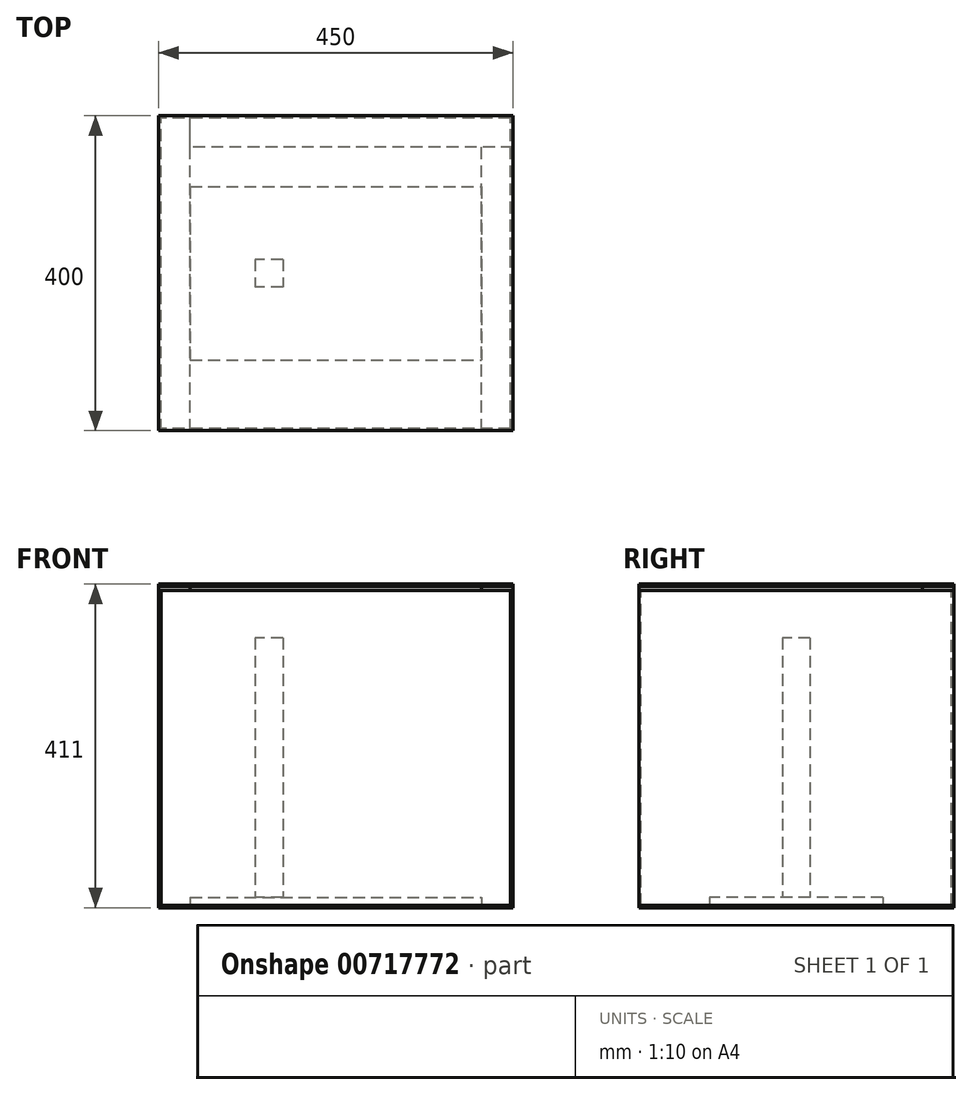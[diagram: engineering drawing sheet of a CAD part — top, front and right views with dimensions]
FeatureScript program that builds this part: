
annotation { "Feature Type Name" : "Feature", "Feature Type Description" : "" }
export const myFeature = defineFeature(function(context is Context, id is Id, definition is map)
    precondition{}
    {
        {
            assignVariable(context, id + "F0", {"name" : "t", "anyValue" : 3});
        }
        {
            var Q0;
            Q0=qCreatedBy(makeId("Top.planeOp"),FACE);
            var sketch = newSketch(context, id + "F1", { "sketchPlane" : qUnion([Q0])});
            skLineSegment(sketch, "E0.bottom", {"start": v(145, 97.5) * mm, "end": v(-145, 97.5) * mm});
            skLineSegment(sketch, "E0.top", {"start": v(145, -97.5) * mm, "end": v(-145, -97.5) * mm});
            skLineSegment(sketch, "E0.left", {"start": v(145, 97.5) * mm, "end": v(145, -97.5) * mm});
            skLineSegment(sketch, "E0.right", {"start": v(-145, 97.5) * mm, "end": v(-145, -97.5) * mm});
            skPoint(sketch, "E0.middle", {"position": v(0, 0) * mm});
            skSolve(sketch);
        }
        {
            var Q0;
            Q0 = qSketchRegion(id + "F1", true);
            extrude(context, id + "F2", {"entities" : qUnion([Q0]), "depth" : 10 * mm, "offsetDistance" : 25 * mm});
        }
        {
            var Q0;
            Q0=qCreatedBy(makeId("Top.planeOp"),FACE);
            var sketch = newSketch(context, id + "F3", { "sketchPlane" : qUnion([Q0])});
            skLineSegment(sketch, "E1.bottom", {"start": v(-185, 110) * mm, "end": v(185, 110) * mm});
            skLineSegment(sketch, "E1.top", {"start": v(-185, -110) * mm, "end": v(185, -110) * mm});
            skLineSegment(sketch, "E1.left", {"start": v(-185, 110) * mm, "end": v(-185, -110) * mm});
            skLineSegment(sketch, "E1.right", {"start": v(185, 110) * mm, "end": v(185, -110) * mm});
            skPoint(sketch, "E1.middle", {"position": v(0, 0) * mm});
            skSolve(sketch);
        }
        {
            var Q0;
            Q0 = qSketchRegion(id + "F3", true);
            extrude(context, id + "F4", {"entities" : qUnion([Q0]), "depth" : 10 * mm, "offsetDistance" : 25 * mm});
        }
        {
            var Q0;
            Q0=makeQuery(id+"F4.opExtrude","CAP_FACE",FACE,{"disambiguationData":[OSD([sQuery(id+"F3.wireOp",EDGE,"E1.bottom"),sQuery(id+"F3.wireOp",EDGE,"E1.top"),sQuery(id+"F3.wireOp",EDGE,"E1.left"),sQuery(id+"F3.wireOp",EDGE,"E1.right")])],"isStart":false});
            var sketch = newSketch(context, id + "F5", { "sketchPlane" : qUnion([Q0])});
            skLineSegment(sketch, "E2.bottom", {"start": v(-67.27, 17.5) * mm, "end": v(-102.27, 17.5) * mm});
            skLineSegment(sketch, "E2.top", {"start": v(-67.27, -17.5) * mm, "end": v(-102.27, -17.5) * mm});
            skLineSegment(sketch, "E2.left", {"start": v(-67.27, 17.5) * mm, "end": v(-67.27, -17.5) * mm});
            skLineSegment(sketch, "E2.right", {"start": v(-102.27, 17.5) * mm, "end": v(-102.27, -17.5) * mm});
            skPoint(sketch, "E2.middle", {"position": v(-84.77, 0) * mm});
            skSolve(sketch);
        }
        {
            var Q0;
            Q0=makeQuery(id+"F5.imprint","IMPRINT",FACE,{"disambiguationData":[TD([[makeQuery(id+"F5.imprint","IMPRINT",EDGE,{"derivedFrom":sQuery(id+"F5.wireOp",EDGE,"E2.bottom")}),1.0]])]});
            extrude(context, id + "F6", {"entities" : qUnion([Q0]), "operationType" : NewBodyOperationType.ADD, "depth" : 330 * mm, "offsetDistance" : 25 * mm});
        }
        {
            var Q0;
            Q0=qCreatedBy(makeId("Top.planeOp"),FACE);
            var sketch = newSketch(context, id + "F7", { "sketchPlane" : qUnion([Q0])});
            skLineSegment(sketch, "E3.bottom", {"start": v(225, -200) * mm, "end": v(-225, -200) * mm});
            skLineSegment(sketch, "E3.top", {"start": v(225, 200) * mm, "end": v(-225, 200) * mm});
            skLineSegment(sketch, "E3.left", {"start": v(225, -200) * mm, "end": v(225, 200) * mm});
            skLineSegment(sketch, "E3.right", {"start": v(-225, -200) * mm, "end": v(-225, 200) * mm});
            skPoint(sketch, "E3.middle", {"position": v(0, 0) * mm});
            skSolve(sketch);
        }
        {
            var Q0;
            Q0 = qSketchRegion(id + "F7", true);
            extrude(context, id + "F8", {"entities" : qUnion([Q0]), "oppositeDirection" : true, "depth" : (getVariable(context, 't')) * mm, "offsetDistance" : 25 * mm});
        }
        {
            var Q0;
            Q0=makeQuery(id+"F8.opExtrude","SWEPT_FACE",FACE,{"disambiguationData":[OSD([sQuery(id+"F7.wireOp",EDGE,"E3.right")])]});
            var sketch = newSketch(context, id + "F9", { "sketchPlane" : qUnion([Q0])});
            skLineSegment(sketch, "E4.bottom", {"start": v(-200, 0) * mm, "end": v(200, 0) * mm});
            skLineSegment(sketch, "E4.top", {"start": v(-200, 400) * mm, "end": v(200, 400) * mm});
            skLineSegment(sketch, "E4.left", {"start": v(-200, 0) * mm, "end": v(-200, 400) * mm});
            skLineSegment(sketch, "E4.right", {"start": v(200, 0) * mm, "end": v(200, 400) * mm});
            skSolve(sketch);
        }
        {
            var Q0;
            Q0 = qSketchRegion(id + "F9", true);
            extrude(context, id + "F10", {"entities" : qUnion([Q0]), "oppositeDirection" : true, "depth" : (getVariable(context, 't')) * mm, "offsetDistance" : 25 * mm});
        }
        {
            var Q0;
            Q0=makeQuery(id+"F10.opExtrude","SWEPT_BODY",BODY,{"disambiguationData":[OSD([sQuery(id+"F9.wireOp",EDGE,"E4.bottom"),sQuery(id+"F9.wireOp",EDGE,"E4.top"),sQuery(id+"F9.wireOp",EDGE,"E4.left"),sQuery(id+"F9.wireOp",EDGE,"E4.right")])]});
            var Q1;
            Q1=qCreatedBy(makeId("Right.planeOp"),FACE);
            mirror(context, id + "F11", {"entities" : qUnion([Q0]), "mirrorPlane" : qUnion([Q1])});
        }
        {
            var Q0;
            Q0=makeQuery(id+"F8.opExtrude","SWEPT_FACE",FACE,{"disambiguationData":[OSD([sQuery(id+"F7.wireOp",EDGE,"E3.bottom")])]});
            var sketch = newSketch(context, id + "F12", { "sketchPlane" : qUnion([Q0])});
            skLineSegment(sketch, "E5.bottom", {"start": v(-222, 0) * mm, "end": v(222, 0) * mm});
            skLineSegment(sketch, "E5.top", {"start": v(-222, 400) * mm, "end": v(222, 400) * mm});
            skLineSegment(sketch, "E5.left", {"start": v(-222, 0) * mm, "end": v(-222, 400) * mm});
            skLineSegment(sketch, "E5.right", {"start": v(222, 0) * mm, "end": v(222, 400) * mm});
            skSolve(sketch);
        }
        {
            var Q0;
            Q0 = qSketchRegion(id + "F12", true);
            extrude(context, id + "F13", {"entities" : qUnion([Q0]), "oppositeDirection" : true, "depth" : (getVariable(context, 't')) * mm, "offsetDistance" : 25 * mm});
        }
        {
            var Q0;
            Q0=makeQuery(id+"F13.opExtrude","SWEPT_BODY",BODY,{"disambiguationData":[OSD([sQuery(id+"F12.wireOp",EDGE,"E5.bottom"),sQuery(id+"F12.wireOp",EDGE,"E5.top"),sQuery(id+"F12.wireOp",EDGE,"E5.left"),sQuery(id+"F12.wireOp",EDGE,"E5.right")])]});
            var Q1;
            Q1=qCreatedBy(makeId("Front.planeOp"),FACE);
            mirror(context, id + "F14", {"entities" : qUnion([Q0]), "mirrorPlane" : qUnion([Q1])});
        }
        {
            var Q0;
            Q0=makeQuery(id+"F10.opExtrude","SWEPT_FACE",FACE,{"disambiguationData":[OSD([sQuery(id+"F9.wireOp",EDGE,"E4.top")])]});
            var sketch = newSketch(context, id + "F15", { "sketchPlane" : qUnion([Q0])});
            skLineSegment(sketch, "E6.bottom", {"start": v(-225, -200) * mm, "end": v(-185, -200) * mm});
            skLineSegment(sketch, "E6.top", {"start": v(-225, 200) * mm, "end": v(-185, 200) * mm});
            skLineSegment(sketch, "E6.left", {"start": v(-225, -200) * mm, "end": v(-225, 200) * mm});
            skLineSegment(sketch, "E6.right", {"start": v(-185, -200) * mm, "end": v(-185, 200) * mm});
            skSolve(sketch);
        }
        {
            var Q0;
            Q0 = qSketchRegion(id + "F15", true);
            extrude(context, id + "F16", {"entities" : qUnion([Q0]), "depth" : 5 * mm, "offsetDistance" : 25 * mm});
        }
        {
            var Q0;
            Q0=makeQuery(id+"F16.opExtrude","CAP_FACE",FACE,{"disambiguationData":[OSD([sQuery(id+"F15.wireOp",EDGE,"E6.bottom"),sQuery(id+"F15.wireOp",EDGE,"E6.top"),sQuery(id+"F15.wireOp",EDGE,"E6.left"),sQuery(id+"F15.wireOp",EDGE,"E6.right")])],"isStart":false});
            var sketch = newSketch(context, id + "F17", { "sketchPlane" : qUnion([Q0])});
            skLineSegment(sketch, "E7.bottom", {"start": v(-225, 200) * mm, "end": v(225, 200) * mm});
            skLineSegment(sketch, "E7.top", {"start": v(-225, -200) * mm, "end": v(225, -200) * mm});
            skLineSegment(sketch, "E7.left", {"start": v(-225, 200) * mm, "end": v(-225, -200) * mm});
            skLineSegment(sketch, "E7.right", {"start": v(225, 200) * mm, "end": v(225, -200) * mm});
            skSolve(sketch);
        }
        {
            var Q0;
            Q0 = qSketchRegion(id + "F17", true);
            extrude(context, id + "F18", {"entities" : qUnion([Q0]), "depth" : (getVariable(context, 't')) * mm, "offsetDistance" : 25 * mm});
        }
        {
            var Q0;
            Q0=makeQuery(id+"F16.opExtrude","CAP_FACE",FACE,{"disambiguationData":[OSD([sQuery(id+"F15.wireOp",EDGE,"E6.bottom"),sQuery(id+"F15.wireOp",EDGE,"E6.top"),sQuery(id+"F15.wireOp",EDGE,"E6.left"),sQuery(id+"F15.wireOp",EDGE,"E6.right")])],"isStart":true});
            var sketch = newSketch(context, id + "F19", { "sketchPlane" : qUnion([Q0])});
            skLineSegment(sketch, "E8.bottom", {"start": v(225, -200) * mm, "end": v(-185, -200) * mm});
            skLineSegment(sketch, "E8.top", {"start": v(225, -160) * mm, "end": v(-185, -160) * mm});
            skLineSegment(sketch, "E8.left", {"start": v(225, -200) * mm, "end": v(225, -160) * mm});
            skLineSegment(sketch, "E8.right", {"start": v(-185, -200) * mm, "end": v(-185, -160) * mm});
            skSolve(sketch);
        }
        {
            var Q0;
            Q0 = qSketchRegion(id + "F19", true);
            var Q1;
            Q1=makeQuery(id+"F16.opExtrude","CAP_FACE",FACE,{"disambiguationData":[OSD([sQuery(id+"F15.wireOp",EDGE,"E6.bottom"),sQuery(id+"F15.wireOp",EDGE,"E6.top"),sQuery(id+"F15.wireOp",EDGE,"E6.left"),sQuery(id+"F15.wireOp",EDGE,"E6.right")])],"isStart":false});
            extrude(context, id + "F20", {"entities" : qUnion([Q0]), "endBound" : BoundingType.UP_TO_SURFACE, "oppositeDirection" : true, "depth" : 25 * mm, "endBoundEntityFace" : qUnion([Q1]), "offsetDistance" : 25 * mm});
        }
        {
            var Q0;
            Q0=makeQuery(id+"F20.opExtrude","CAP_FACE",FACE,{"disambiguationData":[OSD([sQuery(id+"F19.wireOp",EDGE,"E8.bottom"),sQuery(id+"F19.wireOp",EDGE,"E8.top"),sQuery(id+"F19.wireOp",EDGE,"E8.left"),sQuery(id+"F19.wireOp",EDGE,"E8.right")])],"isStart":true});
            var sketch = newSketch(context, id + "F21", { "sketchPlane" : qUnion([Q0])});
            skLineSegment(sketch, "E9.bottom", {"start": v(225, 200) * mm, "end": v(185, 200) * mm});
            skLineSegment(sketch, "E9.top", {"start": v(225, -160) * mm, "end": v(185, -160) * mm});
            skLineSegment(sketch, "E9.left", {"start": v(225, 200) * mm, "end": v(225, -160) * mm});
            skLineSegment(sketch, "E9.right", {"start": v(185, 200) * mm, "end": v(185, -160) * mm});
            skSolve(sketch);
        }
        {
            var Q0;
            Q0 = qSketchRegion(id + "F21", true);
            var Q1;
            Q1=makeQuery(id+"F20.opExtrude","CAP_FACE",FACE,{"disambiguationData":[OSD([sQuery(id+"F19.wireOp",EDGE,"E8.bottom"),sQuery(id+"F19.wireOp",EDGE,"E8.top"),sQuery(id+"F19.wireOp",EDGE,"E8.left"),sQuery(id+"F19.wireOp",EDGE,"E8.right")])],"isStart":false});
            extrude(context, id + "F22", {"entities" : qUnion([Q0]), "endBound" : BoundingType.UP_TO_SURFACE, "oppositeDirection" : true, "depth" : 25 * mm, "endBoundEntityFace" : qUnion([Q1]), "offsetDistance" : 25 * mm});
        }
    });
